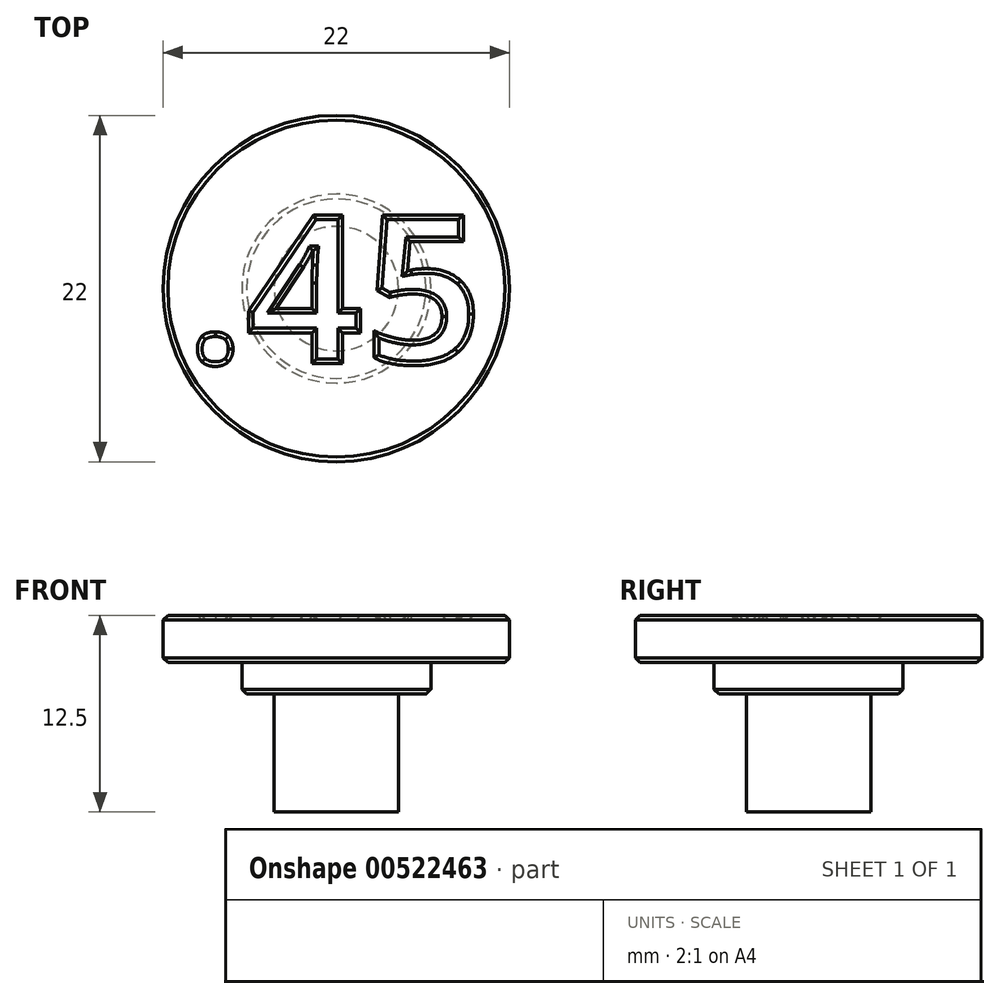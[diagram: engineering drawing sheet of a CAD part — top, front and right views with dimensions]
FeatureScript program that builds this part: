
annotation { "Feature Type Name" : "Feature", "Feature Type Description" : "" }
export const myFeature = defineFeature(function(context is Context, id is Id, definition is map)
    precondition{}
    {
        {
            var Q0;
            Q0=qCreatedBy(makeId("Top.planeOp"),FACE);
            var sketch = newSketch(context, id + "F0", { "sketchPlane" : qUnion([Q0])});
            skCircle(sketch, "E0", {"center": v(0, 0) * mm, "radius": 3.95 * mm});
            skSolve(sketch);
        }
        {
            var Q0;
            Q0=makeQuery(id+"F0.imprint","IMPRINT",FACE,{"disambiguationData":[TD([[makeQuery(id+"F0.imprint","IMPRINT",EDGE,{"derivedFrom":sQuery(id+"F0.wireOp",EDGE,"E0")}),1.0]])]});
            extrude(context, id + "F1", {"entities" : qUnion([Q0]), "depth" : 7.5 * mm, "offsetDistance" : 25 * mm});
        }
        {
            var Q0;
            Q0=makeQuery(id+"F1.opExtrude","CAP_FACE",FACE,{"disambiguationData":[OSD([sQuery(id+"F0.wireOp",EDGE,"E0")])],"isStart":false});
            var sketch = newSketch(context, id + "F2", { "sketchPlane" : qUnion([Q0])});
            skCircle(sketch, "E1", {"center": v(0, 0) * mm, "radius": 6 * mm});
            skSolve(sketch);
        }
        {
            var Q0;
            Q0=makeQuery(id+"F2.imprint","IMPRINT",FACE,{"disambiguationData":[TD([[makeQuery(id+"F2.imprint","IMPRINT",EDGE,{"derivedFrom":sQuery(id+"F2.wireOp",EDGE,"E1")}),1.0]])]});
            var Q1;
            Q1=makeQuery(id+"F2.imprint","IMPRINT",FACE,{"disambiguationData":[TD([[makeQuery(id+"F2.imprint","IMPRINT",EDGE,{"derivedFrom":makeQuery(id+"F1.opExtrude","CAP_EDGE",EDGE,{"disambiguationData":[OSD([sQuery(id+"F0.wireOp",EDGE,"E0")])],"isStart":false})}),1.0]])]});
            extrude(context, id + "F3", {"entities" : qUnion([Q0, Q1]), "operationType" : NewBodyOperationType.ADD, "depth" : 2 * mm, "offsetDistance" : 25 * mm});
        }
        {
            var Q0;
            Q0=makeQuery(id+"F3.opExtrude","CAP_FACE",FACE,{"disambiguationData":[OSD([sQuery(id+"F2.wireOp",EDGE,"E1")])],"isStart":false});
            var sketch = newSketch(context, id + "F4", { "sketchPlane" : qUnion([Q0])});
            skCircle(sketch, "E2", {"center": v(0, 0) * mm, "radius": 11 * mm});
            skSolve(sketch);
        }
        {
            var Q0;
            Q0=makeQuery(id+"F4.imprint","IMPRINT",FACE,{"disambiguationData":[TD([[makeQuery(id+"F4.imprint","IMPRINT",EDGE,{"derivedFrom":makeQuery(id+"F3.opExtrude","CAP_EDGE",EDGE,{"disambiguationData":[OSD([sQuery(id+"F2.wireOp",EDGE,"E1")])],"isStart":false})}),1.0]])]});
            var Q1;
            Q1=makeQuery(id+"F4.imprint","IMPRINT",FACE,{"disambiguationData":[TD([[makeQuery(id+"F4.imprint","IMPRINT",EDGE,{"derivedFrom":sQuery(id+"F4.wireOp",EDGE,"E2")}),1.0]])]});
            extrude(context, id + "F5", {"entities" : qUnion([Q0, Q1]), "operationType" : NewBodyOperationType.ADD, "depth" : 3 * mm, "offsetDistance" : 25 * mm});
        }
        {
            var Q0;
            Q0=makeQuery(id+"F5.opExtrude","SWEPT_FACE",FACE,{"disambiguationData":[OSD([sQuery(id+"F4.wireOp",EDGE,"E2")])]});
            chamfer(context, id + "F6", {"entities" : qUnion([Q0]), "width" : 0.3 * mm, "tangentPropagation" : true});
        }
        {
            var Q0;
            Q0=makeQuery(id+"F3.opExtrude","CAP_EDGE",EDGE,{"disambiguationData":[OSD([sQuery(id+"F2.wireOp",EDGE,"E1")])],"isStart":true});
            chamfer(context, id + "F7", {"entities" : qUnion([Q0]), "width" : .3 * mm, "tangentPropagation" : true});
        }
        {
            var Q0;
            Q0=makeQuery(id+"F5.opExtrude","CAP_FACE",FACE,{"disambiguationData":[OSD([sQuery(id+"F4.wireOp",EDGE,"E2")])],"isStart":false});
            var sketch = newSketch(context, id + "F8", { "sketchPlane" : qUnion([Q0])});
            skText(sketch, "E3", { "text": ".45", "fontName": "OpenSans-Bold.ttf"});
            skLineSegment(sketch, "E4", {"start": v(0, 4.77) * mm, "end": v(0, -4.77) * mm, "construction": true});
            skLineSegment(sketch, "E5", {"start": v(-9.58, 0) * mm, "end": v(9.58, 0) * mm, "construction": true});
            skPoint(sketch, "E6", {"position": v(0, 0) * mm});
            const initialGuessF8  = {"E3": [-0.00958, -0.00477, 1, 0, 0.00953]};
            skSetInitialGuess(sketch, initialGuessF8);
            skSolve(sketch);
        }
        {
            var Q0;
            Q0=makeQuery(id+"F8.imprint","IMPRINT",FACE,{"disambiguationData":[TD([[makeQuery(id+"F8.imprint","IMPRINT",EDGE,{"derivedFrom":sQuery(id+"F8.wireOp",EDGE,"E3.sketch_text.stroke-8")}),-1.0]])]});
            var Q1;
            Q1=makeQuery(id+"F8.imprint","IMPRINT",FACE,{"disambiguationData":[TD([[makeQuery(id+"F8.imprint","IMPRINT",EDGE,{"derivedFrom":sQuery(id+"F8.wireOp",EDGE,"E3.sketch_text.stroke-26")}),-1.0]])]});
            var Q2;
            Q2=makeQuery(id+"F8.imprint","IMPRINT",FACE,{"disambiguationData":[TD([[makeQuery(id+"F8.imprint","IMPRINT",EDGE,{"derivedFrom":sQuery(id+"F8.wireOp",EDGE,"E3.sketch_text.stroke-0")}),-1.0]])]});
            extrude(context, id + "F9", {"entities" : qUnion([Q0, Q1, Q2]), "operationType" : NewBodyOperationType.REMOVE, "oppositeDirection" : true, "depth" : 0.3 * mm, "offsetDistance" : 25 * mm});
        }
        {
            var Q0;
            Q0=makeQuery(id+"F9.boolean.opBoolean","COPY",FACE,{"derivedFrom":makeQuery(id+"F9.opExtrude","CAP_FACE",FACE,{"disambiguationData":[OSD([sQuery(id+"F8.wireOp",EDGE,"E3.sketch_text.stroke-8"),sQuery(id+"F8.wireOp",EDGE,"E3.sketch_text.stroke-9"),sQuery(id+"F8.wireOp",EDGE,"E3.sketch_text.stroke-10"),sQuery(id+"F8.wireOp",EDGE,"E3.sketch_text.stroke-11"),sQuery(id+"F8.wireOp",EDGE,"E3.sketch_text.stroke-12"),sQuery(id+"F8.wireOp",EDGE,"E3.sketch_text.stroke-13"),sQuery(id+"F8.wireOp",EDGE,"E3.sketch_text.stroke-14"),sQuery(id+"F8.wireOp",EDGE,"E3.sketch_text.stroke-15"),sQuery(id+"F8.wireOp",EDGE,"E3.sketch_text.stroke-16"),sQuery(id+"F8.wireOp",EDGE,"E3.sketch_text.stroke-17"),sQuery(id+"F8.wireOp",EDGE,"E3.sketch_text.stroke-18"),sQuery(id+"F8.wireOp",EDGE,"E3.sketch_text.stroke-19"),sQuery(id+"F8.wireOp",EDGE,"E3.sketch_text.stroke-20"),sQuery(id+"F8.wireOp",EDGE,"E3.sketch_text.stroke-21"),sQuery(id+"F8.wireOp",EDGE,"E3.sketch_text.stroke-22"),sQuery(id+"F8.wireOp",EDGE,"E3.sketch_text.stroke-23"),sQuery(id+"F8.wireOp",EDGE,"E3.sketch_text.stroke-24"),sQuery(id+"F8.wireOp",EDGE,"E3.sketch_text.stroke-25")])],"isStart":false})});
            var Q1;
            Q1=makeQuery(id+"F9.boolean.opBoolean","COPY",FACE,{"derivedFrom":makeQuery(id+"F9.opExtrude","CAP_FACE",FACE,{"disambiguationData":[OSD([sQuery(id+"F8.wireOp",EDGE,"E3.sketch_text.stroke-0"),sQuery(id+"F8.wireOp",EDGE,"E3.sketch_text.stroke-1"),sQuery(id+"F8.wireOp",EDGE,"E3.sketch_text.stroke-2"),sQuery(id+"F8.wireOp",EDGE,"E3.sketch_text.stroke-3"),sQuery(id+"F8.wireOp",EDGE,"E3.sketch_text.stroke-4"),sQuery(id+"F8.wireOp",EDGE,"E3.sketch_text.stroke-5"),sQuery(id+"F8.wireOp",EDGE,"E3.sketch_text.stroke-6"),sQuery(id+"F8.wireOp",EDGE,"E3.sketch_text.stroke-7")])],"isStart":false})});
            var Q2;
            Q2=makeQuery(id+"F9.boolean.opBoolean","COPY",FACE,{"derivedFrom":makeQuery(id+"F9.opExtrude","CAP_FACE",FACE,{"disambiguationData":[OSD([sQuery(id+"F8.wireOp",EDGE,"E3.sketch_text.stroke-26"),sQuery(id+"F8.wireOp",EDGE,"E3.sketch_text.stroke-27"),sQuery(id+"F8.wireOp",EDGE,"E3.sketch_text.stroke-28"),sQuery(id+"F8.wireOp",EDGE,"E3.sketch_text.stroke-29"),sQuery(id+"F8.wireOp",EDGE,"E3.sketch_text.stroke-30"),sQuery(id+"F8.wireOp",EDGE,"E3.sketch_text.stroke-31"),sQuery(id+"F8.wireOp",EDGE,"E3.sketch_text.stroke-32"),sQuery(id+"F8.wireOp",EDGE,"E3.sketch_text.stroke-33"),sQuery(id+"F8.wireOp",EDGE,"E3.sketch_text.stroke-34"),sQuery(id+"F8.wireOp",EDGE,"E3.sketch_text.stroke-35"),sQuery(id+"F8.wireOp",EDGE,"E3.sketch_text.stroke-36"),sQuery(id+"F8.wireOp",EDGE,"E3.sketch_text.stroke-37"),sQuery(id+"F8.wireOp",EDGE,"E3.sketch_text.stroke-38"),sQuery(id+"F8.wireOp",EDGE,"E3.sketch_text.stroke-39"),sQuery(id+"F8.wireOp",EDGE,"E3.sketch_text.stroke-40"),sQuery(id+"F8.wireOp",EDGE,"E3.sketch_text.stroke-41"),sQuery(id+"F8.wireOp",EDGE,"E3.sketch_text.stroke-42"),sQuery(id+"F8.wireOp",EDGE,"E3.sketch_text.stroke-43"),sQuery(id+"F8.wireOp",EDGE,"E3.sketch_text.stroke-44"),sQuery(id+"F8.wireOp",EDGE,"E3.sketch_text.stroke-45")])],"isStart":false})});
            chamfer(context, id + "F10", {"entities" : qUnion([Q0, Q1, Q2]), "width" : 0.3 * mm, "tangentPropagation" : true});
        }
    });
